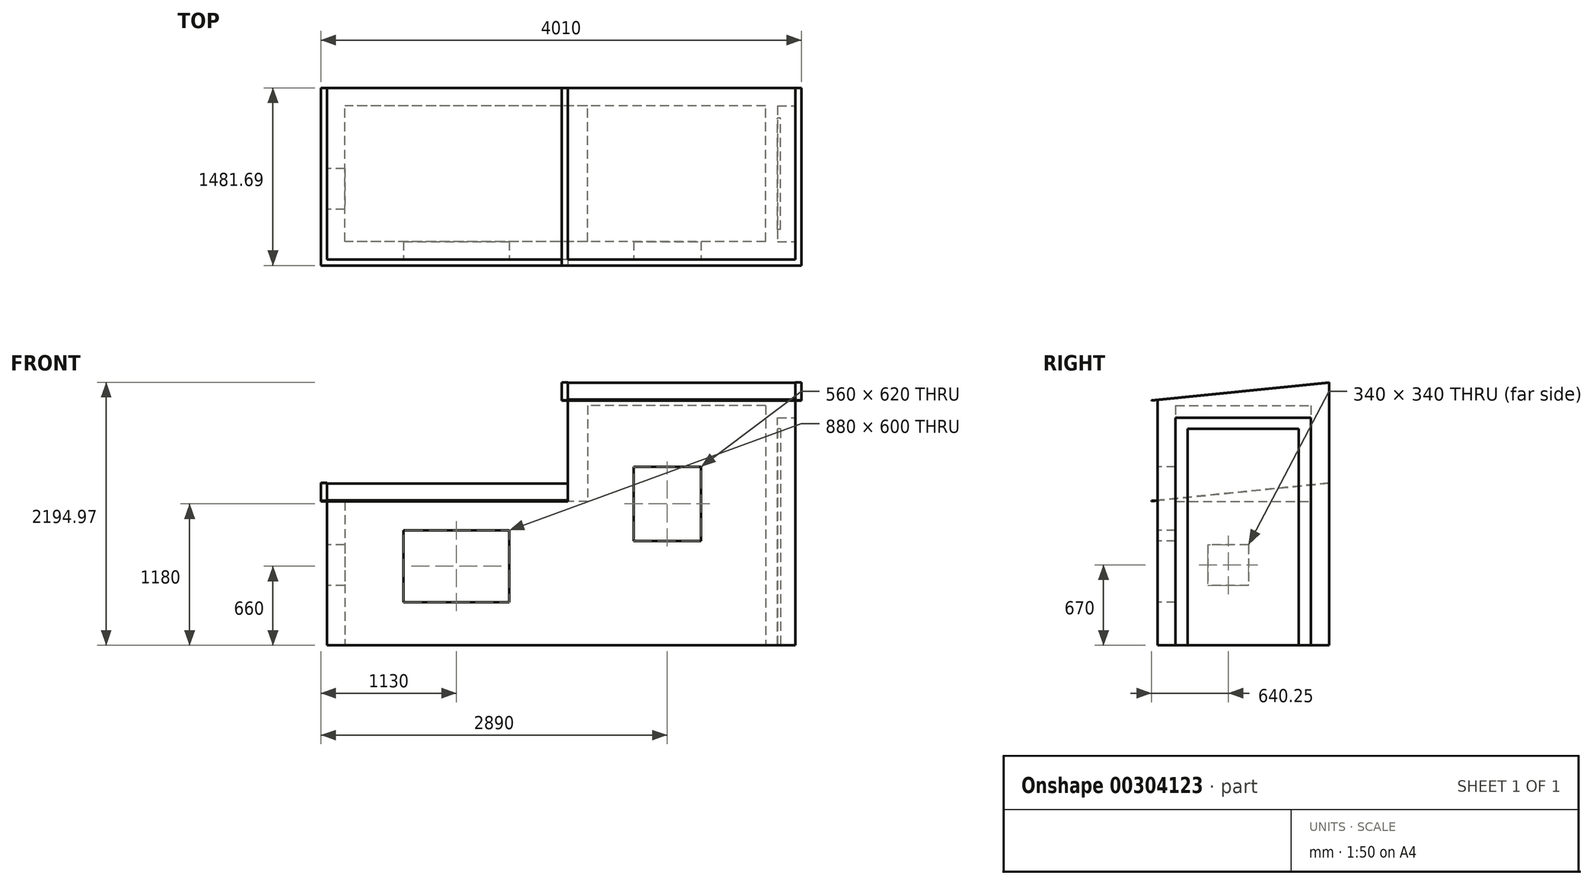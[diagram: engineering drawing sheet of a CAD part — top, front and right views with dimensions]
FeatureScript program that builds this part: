
annotation { "Feature Type Name" : "Feature", "Feature Type Description" : "" }
export const myFeature = defineFeature(function(context is Context, id is Id, definition is map)
    precondition{}
    {
        {
            var Q0;
            Q0=qCreatedBy(makeId("Top.planeOp"),FACE);
            var sketch = newSketch(context, id + "F0", { "sketchPlane" : qUnion([Q0])});
            skLineSegment(sketch, "E0.bottom", {"start": v(402.3, 703.13) * mm, "end": v(2302.3, 703.13) * mm});
            skLineSegment(sketch, "E0.top", {"start": v(402.3, -728.31) * mm, "end": v(2302.3, -728.31) * mm});
            skLineSegment(sketch, "E0.left", {"start": v(402.3, 703.13) * mm, "end": v(402.3, -728.31) * mm});
            skLineSegment(sketch, "E0.right", {"start": v(2302.3, 703.13) * mm, "end": v(2302.3, -728.31) * mm});
            skLineSegment(sketch, "E1.bottom", {"start": v(402.3, 703.13) * mm, "end": v(-1607.7, 703.13) * mm});
            skLineSegment(sketch, "E1.top", {"start": v(402.3, -728.31) * mm, "end": v(-1607.7, -728.31) * mm});
            skLineSegment(sketch, "E1.right", {"start": v(-1607.7, 703.13) * mm, "end": v(-1607.7, -728.31) * mm});
            skSolve(sketch);
        }
        {
            var Q0;
            Q0=makeQuery(id+"F0.imprint","IMPRINT",FACE,{"disambiguationData":[TD([[makeQuery(id+"F0.imprint","IMPRINT",EDGE,{"derivedFrom":sQuery(id+"F0.wireOp",EDGE,"E0.bottom")}),-1.0]])]});
            extrude(context, id + "F1", {"entities" : qUnion([Q0]), "depth" : 2190 * mm, "offsetDistance" : 25 * mm});
        }
        {
            var Q0;
            Q0=makeQuery(id+"F0.imprint","IMPRINT",FACE,{"disambiguationData":[TD([[makeQuery(id+"F0.imprint","IMPRINT",EDGE,{"derivedFrom":sQuery(id+"F0.wireOp",EDGE,"E1.bottom")}),1.0]])]});
            extrude(context, id + "F2", {"entities" : qUnion([Q0]), "operationType" : NewBodyOperationType.ADD, "depth" : 1350 * mm, "offsetDistance" : 25 * mm});
        }
        {
            var Q0;
            Q0=makeQuery(id+"F1.opExtrude","SWEPT_FACE",FACE,{"disambiguationData":[OSD([sQuery(id+"F0.wireOp",EDGE,"E0.right")])]});
            var sketch = newSketch(context, id + "F3", { "sketchPlane" : qUnion([Q0])});
            skLineSegment(sketch, "E2.bottom", {"start": v(-578.31, 0) * mm, "end": v(553.13, 0) * mm});
            skLineSegment(sketch, "E2.top", {"start": v(-578.31, 1900) * mm, "end": v(553.13, 1900) * mm});
            skLineSegment(sketch, "E2.left", {"start": v(-578.31, 0) * mm, "end": v(-578.31, 1900) * mm});
            skLineSegment(sketch, "E2.right", {"start": v(553.13, 0) * mm, "end": v(553.13, 1900) * mm});
            skSolve(sketch);
        }
        {
            var Q0;
            Q0=makeQuery(id+"F3.imprint","IMPRINT",FACE,{"disambiguationData":[TD([[makeQuery(id+"F3.imprint","IMPRINT",EDGE,{"derivedFrom":sQuery(id+"F3.wireOp",EDGE,"E2.bottom")}),-1.0]])]});
            extrude(context, id + "F4", {"entities" : qUnion([Q0]), "operationType" : NewBodyOperationType.REMOVE, "oppositeDirection" : true, "depth" : 150 * mm, "offsetDistance" : 25 * mm});
        }
        {
            var Q0;
            Q0=makeQuery(id+"F1.opExtrude","SWEPT_FACE",FACE,{"disambiguationData":[OSD([sQuery(id+"F0.wireOp",EDGE,"E0.right")])]});
            var sketch = newSketch(context, id + "F5", { "sketchPlane" : qUnion([Q0])});
            skLineSegment(sketch, "E3", {"start": v(703.13, 2190) * mm, "end": v(-728.31, 2045.69) * mm});
            skLineSegment(sketch, "E4", {"start": v(-728.31, 2045.69) * mm, "end": v(-728.31, 2190) * mm});
            skLineSegment(sketch, "E5", {"start": v(-728.31, 2190) * mm, "end": v(703.13, 2190) * mm});
            skSolve(sketch);
        }
        {
            var Q0;
            Q0=makeQuery(id+"F5.imprint","IMPRINT",FACE,{"disambiguationData":[TD([[makeQuery(id+"F5.imprint","IMPRINT",EDGE,{"derivedFrom":sQuery(id+"F5.wireOp",EDGE,"E3")}),-1.0]])]});
            extrude(context, id + "F6", {"entities" : qUnion([Q0]), "operationType" : NewBodyOperationType.REMOVE, "oppositeDirection" : true, "depth" : 1900 * mm, "offsetDistance" : 25 * mm});
        }
        {
            var Q0;
            Q0=makeQuery(id+"F2.opExtrude","SWEPT_FACE",FACE,{"disambiguationData":[OSD([sQuery(id+"F0.wireOp",EDGE,"E1.right")])]});
            var sketch = newSketch(context, id + "F7", { "sketchPlane" : qUnion([Q0])});
            skLineSegment(sketch, "E6", {"start": v(-703.13, 1350) * mm, "end": v(728.31, 1205.69) * mm});
            skLineSegment(sketch, "E7", {"start": v(728.31, 1205.69) * mm, "end": v(728.31, 1350) * mm});
            skLineSegment(sketch, "E8", {"start": v(728.31, 1350) * mm, "end": v(-703.13, 1350) * mm});
            skSolve(sketch);
        }
        {
            var Q0;
            Q0=makeQuery(id+"F7.imprint","IMPRINT",FACE,{"disambiguationData":[TD([[makeQuery(id+"F7.imprint","IMPRINT",EDGE,{"derivedFrom":sQuery(id+"F7.wireOp",EDGE,"E6")}),1.0]])]});
            extrude(context, id + "F8", {"entities" : qUnion([Q0]), "operationType" : NewBodyOperationType.REMOVE, "oppositeDirection" : true, "depth" : 2010 * mm, "offsetDistance" : 25 * mm});
        }
        {
            var Q0;
            {var subQ0=sQuery(id+"F0.wireOp",EDGE,"E0.left");Q0=makeQuery(id+"F2.boolean.opBoolean","MERGE",FACE,{"derivedFrom":[makeQuery(id+"F1.opExtrude","CAP_FACE",FACE,{"disambiguationData":[OSD([sQuery(id+"F0.wireOp",EDGE,"E0.bottom"),sQuery(id+"F0.wireOp",EDGE,"E0.top"),sQuery(id+"F0.wireOp",EDGE,"E0.right"),subQ0])],"isStart":true}),makeQuery(id+"F2.opExtrude","CAP_FACE",FACE,{"disambiguationData":[OSD([sQuery(id+"F0.wireOp",EDGE,"E1.bottom"),sQuery(id+"F0.wireOp",EDGE,"E1.top"),subQ0,sQuery(id+"F0.wireOp",EDGE,"E1.right")])],"isStart":true})]});}
            var sketch = newSketch(context, id + "F9", { "sketchPlane" : qUnion([Q0])});
            skLineSegment(sketch, "E9.bottom", {"start": v(2052.3, 578.31) * mm, "end": v(-1457.7, 578.31) * mm});
            skLineSegment(sketch, "E9.top", {"start": v(2052.3, -553.13) * mm, "end": v(-1457.7, -553.13) * mm});
            skLineSegment(sketch, "E9.left", {"start": v(2052.3, 578.31) * mm, "end": v(2052.3, -553.13) * mm});
            skLineSegment(sketch, "E9.right", {"start": v(-1457.7, 578.31) * mm, "end": v(-1457.7, -553.13) * mm});
            skSolve(sketch);
        }
        {
            var Q0;
            Q0=makeQuery(id+"F9.imprint","IMPRINT",FACE,{"disambiguationData":[TD([[makeQuery(id+"F9.imprint","IMPRINT",EDGE,{"derivedFrom":sQuery(id+"F9.wireOp",EDGE,"E9.bottom")}),1.0]])]});
            extrude(context, id + "F10", {"entities" : qUnion([Q0]), "operationType" : NewBodyOperationType.REMOVE, "oppositeDirection" : true, "depth" : 1200 * mm, "offsetDistance" : 25 * mm});
        }
        {
            var Q0;
            Q0=makeQuery(id+"F10.boolean.opBoolean","COPY",FACE,{"derivedFrom":makeQuery(id+"F10.opExtrude","CAP_FACE",FACE,{"disambiguationData":[OSD([sQuery(id+"F9.wireOp",EDGE,"E9.bottom"),sQuery(id+"F9.wireOp",EDGE,"E9.top"),sQuery(id+"F9.wireOp",EDGE,"E9.left"),sQuery(id+"F9.wireOp",EDGE,"E9.right")])],"isStart":false})});
            var sketch = newSketch(context, id + "F11", { "sketchPlane" : qUnion([Q0])});
            skLineSegment(sketch, "E10.bottom", {"start": v(2052.3, 578.31) * mm, "end": v(568.07, 578.31) * mm});
            skLineSegment(sketch, "E10.top", {"start": v(2052.3, -553.13) * mm, "end": v(568.07, -553.13) * mm});
            skLineSegment(sketch, "E10.left", {"start": v(2052.3, 578.31) * mm, "end": v(2052.3, -553.13) * mm});
            skLineSegment(sketch, "E10.right", {"start": v(568.07, 578.31) * mm, "end": v(568.07, -553.13) * mm});
            skSolve(sketch);
        }
        {
            var Q0;
            Q0=makeQuery(id+"F11.imprint","IMPRINT",FACE,{"disambiguationData":[TD([[makeQuery(id+"F11.imprint","IMPRINT",EDGE,{"derivedFrom":sQuery(id+"F11.wireOp",EDGE,"E10.bottom")}),1.0]])]});
            extrude(context, id + "F12", {"entities" : qUnion([Q0]), "operationType" : NewBodyOperationType.REMOVE, "oppositeDirection" : true, "depth" : 800 * mm, "offsetDistance" : 25 * mm});
        }
        {
            var Q0;
            Q0=makeQuery(id+"F2.boolean.opBoolean","MERGE",FACE,{"derivedFrom":[makeQuery(id+"F1.opExtrude","SWEPT_FACE",FACE,{"disambiguationData":[OSD([sQuery(id+"F0.wireOp",EDGE,"E0.top")])]}),makeQuery(id+"F2.opExtrude","SWEPT_FACE",FACE,{"disambiguationData":[OSD([sQuery(id+"F0.wireOp",EDGE,"E1.top")])]})]});
            var sketch = newSketch(context, id + "F13", { "sketchPlane" : qUnion([Q0])});
            skLineSegment(sketch, "E11.bottom", {"start": v(-967.7, 960) * mm, "end": v(-87.7, 960) * mm});
            skLineSegment(sketch, "E11.top", {"start": v(-967.7, 360) * mm, "end": v(-87.7, 360) * mm});
            skLineSegment(sketch, "E11.left", {"start": v(-967.7, 960) * mm, "end": v(-967.7, 360) * mm});
            skLineSegment(sketch, "E11.right", {"start": v(-87.7, 960) * mm, "end": v(-87.7, 360) * mm});
            skLineSegment(sketch, "E12.bottom", {"start": v(952.3, 1490) * mm, "end": v(1512.3, 1490) * mm});
            skLineSegment(sketch, "E12.top", {"start": v(952.3, 870) * mm, "end": v(1512.3, 870) * mm});
            skLineSegment(sketch, "E12.left", {"start": v(952.3, 1490) * mm, "end": v(952.3, 870) * mm});
            skLineSegment(sketch, "E12.right", {"start": v(1512.3, 1490) * mm, "end": v(1512.3, 870) * mm});
            skSolve(sketch);
        }
        {
            var Q0;
            Q0=makeQuery(id+"F13.imprint","IMPRINT",FACE,{"disambiguationData":[TD([[makeQuery(id+"F13.imprint","IMPRINT",EDGE,{"derivedFrom":sQuery(id+"F13.wireOp",EDGE,"E11.bottom")}),-1.0]])]});
            var Q1;
            Q1=makeQuery(id+"F13.imprint","IMPRINT",FACE,{"disambiguationData":[TD([[makeQuery(id+"F13.imprint","IMPRINT",EDGE,{"derivedFrom":sQuery(id+"F13.wireOp",EDGE,"E12.bottom")}),-1.0]])]});
            extrude(context, id + "F14", {"entities" : qUnion([Q0, Q1]), "operationType" : NewBodyOperationType.REMOVE, "oppositeDirection" : true, "depth" : 150 * mm, "offsetDistance" : 25 * mm});
        }
        {
            var Q0;
            Q0=makeQuery(id+"F2.opExtrude","SWEPT_FACE",FACE,{"disambiguationData":[OSD([sQuery(id+"F0.wireOp",EDGE,"E1.right")])]});
            var sketch = newSketch(context, id + "F15", { "sketchPlane" : qUnion([Q0])});
            skLineSegment(sketch, "E13.bottom", {"start": v(-31.69, 840) * mm, "end": v(308.31, 840) * mm});
            skLineSegment(sketch, "E13.top", {"start": v(-31.69, 500) * mm, "end": v(308.31, 500) * mm});
            skLineSegment(sketch, "E13.left", {"start": v(-31.69, 840) * mm, "end": v(-31.69, 500) * mm});
            skLineSegment(sketch, "E13.right", {"start": v(308.31, 840) * mm, "end": v(308.31, 500) * mm});
            skSolve(sketch);
        }
        {
            var Q0;
            Q0=makeQuery(id+"F15.imprint","IMPRINT",FACE,{"disambiguationData":[TD([[makeQuery(id+"F15.imprint","IMPRINT",EDGE,{"derivedFrom":sQuery(id+"F15.wireOp",EDGE,"E13.bottom")}),-1.0]])]});
            extrude(context, id + "F16", {"entities" : qUnion([Q0]), "operationType" : NewBodyOperationType.REMOVE, "oppositeDirection" : true, "depth" : 150 * mm, "offsetDistance" : 25 * mm});
        }
        {
            var Q0;
            Q0=makeQuery(id+"F4.boolean.opBoolean","COPY",FACE,{"derivedFrom":makeQuery(id+"F4.opExtrude","CAP_FACE",FACE,{"disambiguationData":[OSD([sQuery(id+"F3.wireOp",EDGE,"E2.bottom"),sQuery(id+"F3.wireOp",EDGE,"E2.top"),sQuery(id+"F3.wireOp",EDGE,"E2.left"),sQuery(id+"F3.wireOp",EDGE,"E2.right")])],"isStart":false})});
            var sketch = newSketch(context, id + "F17", { "sketchPlane" : qUnion([Q0])});
            skLineSegment(sketch, "E14.bottom", {"start": v(-477.3, 1806) * mm, "end": v(451.47, 1806) * mm});
            skLineSegment(sketch, "E14.top", {"start": v(-477.3, 0) * mm, "end": v(451.47, 0) * mm});
            skLineSegment(sketch, "E14.left", {"start": v(-477.3, 1806) * mm, "end": v(-477.3, 0) * mm});
            skLineSegment(sketch, "E14.right", {"start": v(451.47, 1806) * mm, "end": v(451.47, 0) * mm});
            skSolve(sketch);
        }
        {
            var Q0;
            Q0=makeQuery(id+"F17.imprint","IMPRINT",FACE,{"disambiguationData":[TD([[makeQuery(id+"F17.imprint","IMPRINT",EDGE,{"derivedFrom":sQuery(id+"F17.wireOp",EDGE,"E14.bottom")}),-1.0]])]});
            extrude(context, id + "F18", {"entities" : qUnion([Q0]), "depth" : 25 * mm, "offsetDistance" : 25 * mm});
        }
        {
            var Q0;
            Q0=makeQuery(id+"F6.boolean.opBoolean","COPY",FACE,{"derivedFrom":makeQuery(id+"F6.opExtrude","SWEPT_FACE",FACE,{"disambiguationData":[OSD([sQuery(id+"F5.wireOp",EDGE,"E3")])]})});
            var sketch = newSketch(context, id + "F19", { "sketchPlane" : qUnion([Q0])});
            skLineSegment(sketch, "E15.bottom", {"start": v(2352.3, 919.25) * mm, "end": v(352.3, 919.25) * mm});
            skLineSegment(sketch, "E15.top", {"start": v(2352.3, -569.44) * mm, "end": v(352.3, -569.44) * mm});
            skLineSegment(sketch, "E15.left", {"start": v(2352.3, 919.25) * mm, "end": v(2352.3, -569.44) * mm});
            skLineSegment(sketch, "E15.right", {"start": v(352.3, 919.25) * mm, "end": v(352.3, -569.44) * mm});
            skSolve(sketch);
        }
        {
            var Q0;
            Q0=makeQuery(id+"F19.imprint","IMPRINT",FACE,{"disambiguationData":[TD([[makeQuery(id+"F19.imprint","IMPRINT",EDGE,{"derivedFrom":sQuery(id+"F19.wireOp",EDGE,"E15.top")}),-1.0]])]});
            var Q1;
            {var subQ1=sQuery(id+"F5.wireOp",EDGE,"E3");var subQ3=makeQuery(id+"F6.boolean.opBoolean","COPY",EDGE,{"derivedFrom":makeQuery(id+"F6.opExtrude","CAP_EDGE",EDGE,{"disambiguationData":[OSD([subQ1])],"isStart":true})});Q1=makeQuery(id+"F19.imprint","IMPRINT",FACE,{"disambiguationData":[TD([[makeQuery(id+"F19.imprint","IMPRINT",EDGE,{"derivedFrom":subQ3}),-1.0]])]});}
            extrude(context, id + "F20", {"entities" : qUnion([Q0, Q1]), "depth" : 5 * mm, "offsetDistance" : 25 * mm});
        }
        {
            var Q0;
            Q0=makeQuery(id+"F8.boolean.opBoolean","COPY",FACE,{"derivedFrom":makeQuery(id+"F8.opExtrude","SWEPT_FACE",FACE,{"disambiguationData":[OSD([sQuery(id+"F7.wireOp",EDGE,"E6")])]})});
            var sketch = newSketch(context, id + "F21", { "sketchPlane" : qUnion([Q0])});
            skLineSegment(sketch, "E16.bottom", {"start": v(-1657.7, 835) * mm, "end": v(402.3, 835) * mm});
            skLineSegment(sketch, "E16.top", {"start": v(-1657.7, -653.7) * mm, "end": v(402.3, -653.7) * mm});
            skLineSegment(sketch, "E16.left", {"start": v(-1657.7, 835) * mm, "end": v(-1657.7, -653.7) * mm});
            skLineSegment(sketch, "E16.right", {"start": v(402.3, 835) * mm, "end": v(402.3, -653.7) * mm});
            skSolve(sketch);
        }
        {
            var Q0;
            {var subQ1=sQuery(id+"F7.wireOp",EDGE,"E6");var subQ2=makeQuery(id+"F8.boolean.opBoolean","COPY",EDGE,{"derivedFrom":makeQuery(id+"F8.opExtrude","CAP_EDGE",EDGE,{"disambiguationData":[OSD([subQ1])],"isStart":true})});Q0=makeQuery(id+"F21.imprint","IMPRINT",FACE,{"disambiguationData":[TD([[makeQuery(id+"F21.imprint","IMPRINT",EDGE,{"derivedFrom":subQ2}),1.0]])]});}
            var Q1;
            {var subQ3=sQuery(id+"F21.wireOp",EDGE,"E16.top");Q1=makeQuery(id+"F21.imprint","IMPRINT",FACE,{"disambiguationData":[TD([[makeQuery(id+"F21.imprint","IMPRINT",EDGE,{"derivedFrom":subQ3}),1.0]])]});}
            extrude(context, id + "F22", {"entities" : qUnion([Q0, Q1]), "depth" : 5 * mm, "offsetDistance" : 25 * mm});
        }
    });
